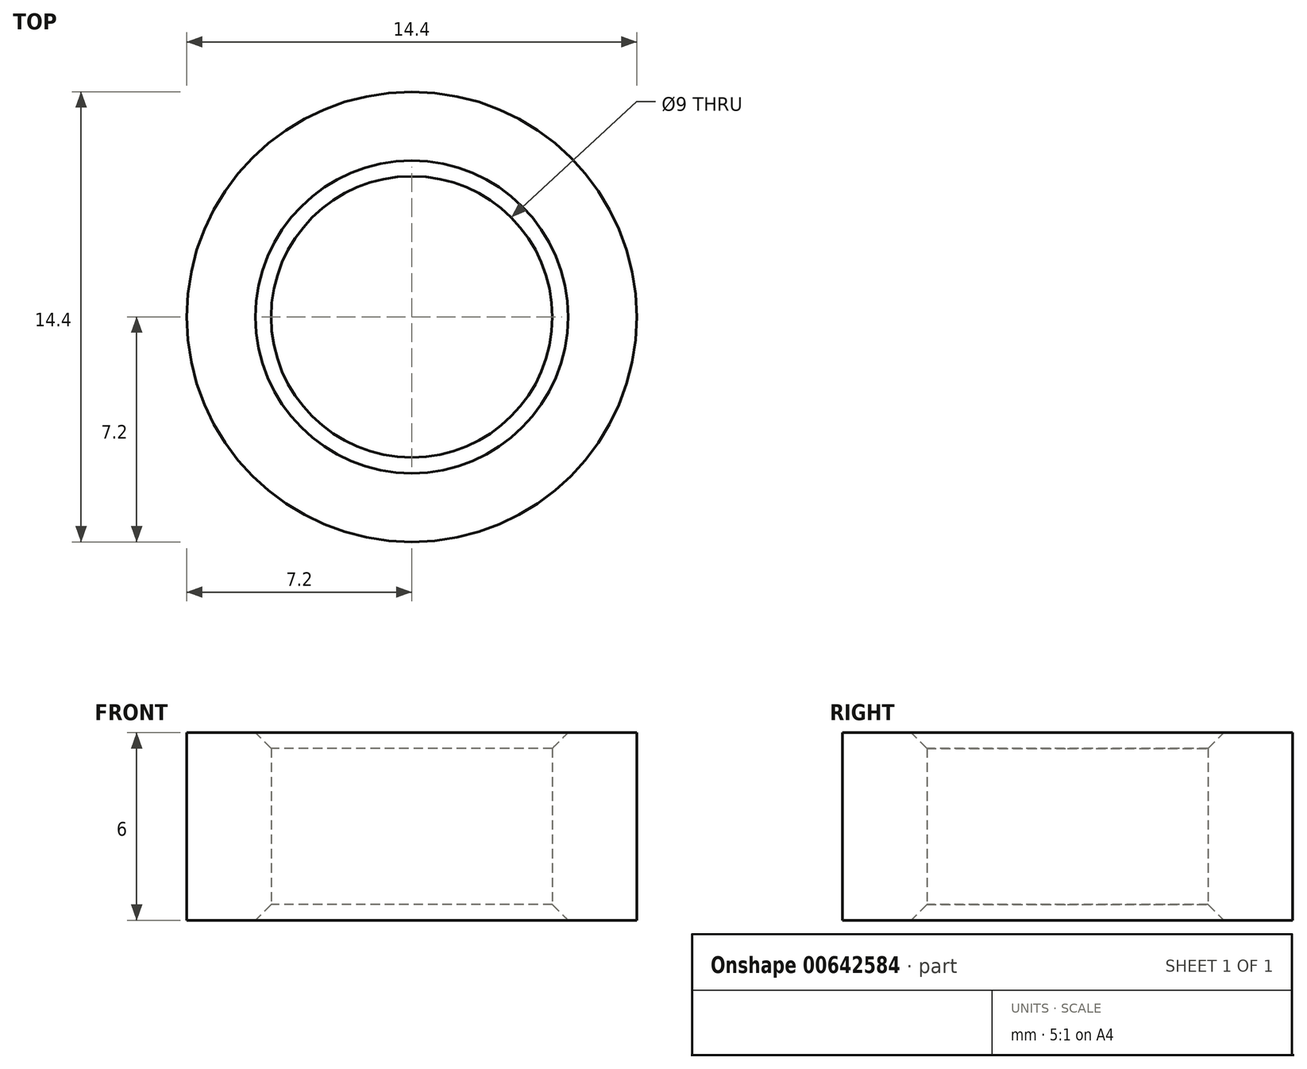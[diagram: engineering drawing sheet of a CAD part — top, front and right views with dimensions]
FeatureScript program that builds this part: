
annotation { "Feature Type Name" : "Feature", "Feature Type Description" : "" }
export const myFeature = defineFeature(function(context is Context, id is Id, definition is map)
    precondition{}
    {
        {
            var Q0;
            Q0=qCreatedBy(makeId("Top.planeOp"),FACE);
            var sketch = newSketch(context, id + "F0", { "sketchPlane" : qUnion([Q0])});
            skCircle(sketch, "E0", {"center": v(0, 0) * mm, "radius": 7.2 * mm});
            skCircle(sketch, "E1", {"center": v(0, 0) * mm, "radius": 4.5 * mm});
            skSolve(sketch);
        }
        {
            var Q0;
            Q0 = qSketchRegion(id + "F0", true);
            extrude(context, id + "F1", {"entities" : qUnion([Q0]), "depth" : 6 * mm, "offsetDistance" : 25 * mm});
        }
        {
            var Q0;
            Q0=makeQuery(id+"F1.opExtrude","CAP_EDGE",EDGE,{"disambiguationData":[OSD([sQuery(id+"F0.wireOp",EDGE,"E1")])],"isStart":false});
            var Q1;
            Q1=makeQuery(id+"F1.opExtrude","CAP_EDGE",EDGE,{"disambiguationData":[OSD([sQuery(id+"F0.wireOp",EDGE,"E1")])],"isStart":true});
            chamfer(context, id + "F2", {"entities" : qUnion([Q0, Q1]), "chamferType" : ChamferType.OFFSET_ANGLE, "width" : 0.5 * mm, "oppositeDirection" : false, "angle" : 45 * degree, "tangentPropagation" : true});
        }
    });
